# Revit family: 2824202
name_source: partatom
category: Lighting Fixtures
revit_build: Autodesk Revit 2017 (Build: 20190507_1515(x64)
units: mm (PartAtom-declared; Revit-internal decimal feet)

## family parameters
Always vertical = Yes
Cut with Voids When Loaded = No
Light Source = Yes
OmniClass Number = 23.80.70.00
OmniClass Title = Lighting
Part Type = Normal
Room Calculation Point = No
Round Connector Dimension = Use Diameter
Shared = No
Work Plane-Based = No

## types (2) — shared parameters
Assembly Code = D5020200
AssetType = Fixed
CHAMF_SYL = 6 mm  [stored 0.019685 ft]
CUTDEPTH_SYL = 38 mm  [stored 0.124672 ft]
CUT_DIST_SYL = 2 mm  [stored 0.00656168 ft]
CUT_WIDT_SYL = 4 mm  [stored 0.0131234 ft]
ClassificationName = Uniclass2015
ClassificationValue = EF_70_80
Color Filter = 16777215
DEPTH_SYL = 120 mm  [stored 0.393701 ft]
Description = -
Dimming Lamp Color Temperature Shift = <None>
DocumentationLiterature = http://www.sylvania-lighting.com
ElectricShockClassification = Class I
HEIGHT_SYL = 63 mm
IfcExportAs = IfcLightFixtureType
IfcExportType = IfcLightFixtureType
ImpactProtectionIndex = IK08
IngressProtection = IP66
Keynote = 16500
Lamp = LED
LampColourRenderingIndex = 80
LampMacAdamStep = 3
LampsType = LED
Manufacturer = Feilo Sylvania
ManufacturerName = Feilo Sylvania
Material_1_FEILO = <By Category>
Material_2_FEILO = <By Category>
Material_3_FEILO = <By Category>
Material_4_FEILO = <By Category>
NominalHeight = 120 mm  [stored 0.393701 ft]
NominalLength = 275 mm
Tilt Angle = -90.00°
URL = http://www.sylvania-lighting.com
Voltage = 0 V
WIDTH_SYL = 138 mm
Weight = 6.8 kg
zero-valued in all types: NominalWidth, PowerFactor

## per-type parameters (varying)
| type | Apparent Load | LampColourTemperature | LampNominalLuminous | LuminousEfficacy | Model | ModelNumber | ModelReference | Name | Photometric Web File | PowerConsumption | TypeName |
| 2824203 MURO RECESSED RECT IP66 450LM 840 GR | 9 VA | 4000 K | 450 lm | 49 lm/W | Muro Recessed Rectangular IP66 450lm 840 Grey | 2824203 | Muro Recessed Rectangular IP66 450lm 840 Grey | Muro Recessed Rectangular IP66 450lm 840 Grey | 2824203_V1.IES | 9.2 W | Muro Recessed Rectangular IP66 450lm 840 Grey |
| 2824202 MURO RECESSED RECT IP66 420LM 830 GR | 10 VA | 3000 K | 420 lm | 44 lm/W | Muro Recessed Rectangular IP66 420lm 830 Grey | 2824202 | Muro Recessed Rectangular IP66 420lm 830 Grey | Muro Recessed Rectangular IP66 420lm 830 Grey | 2824202_V1.IES | 9.5 W | Muro Recessed Rectangular IP66 420lm 830 Grey |

note: [stored X ft] marks values corroborated as IEEE doubles in the binary element streams (Revit-internal decimal feet)

## geometry (parser evidence)
native form markers: Sweep x3
no freeform markers — native parametric forms only
